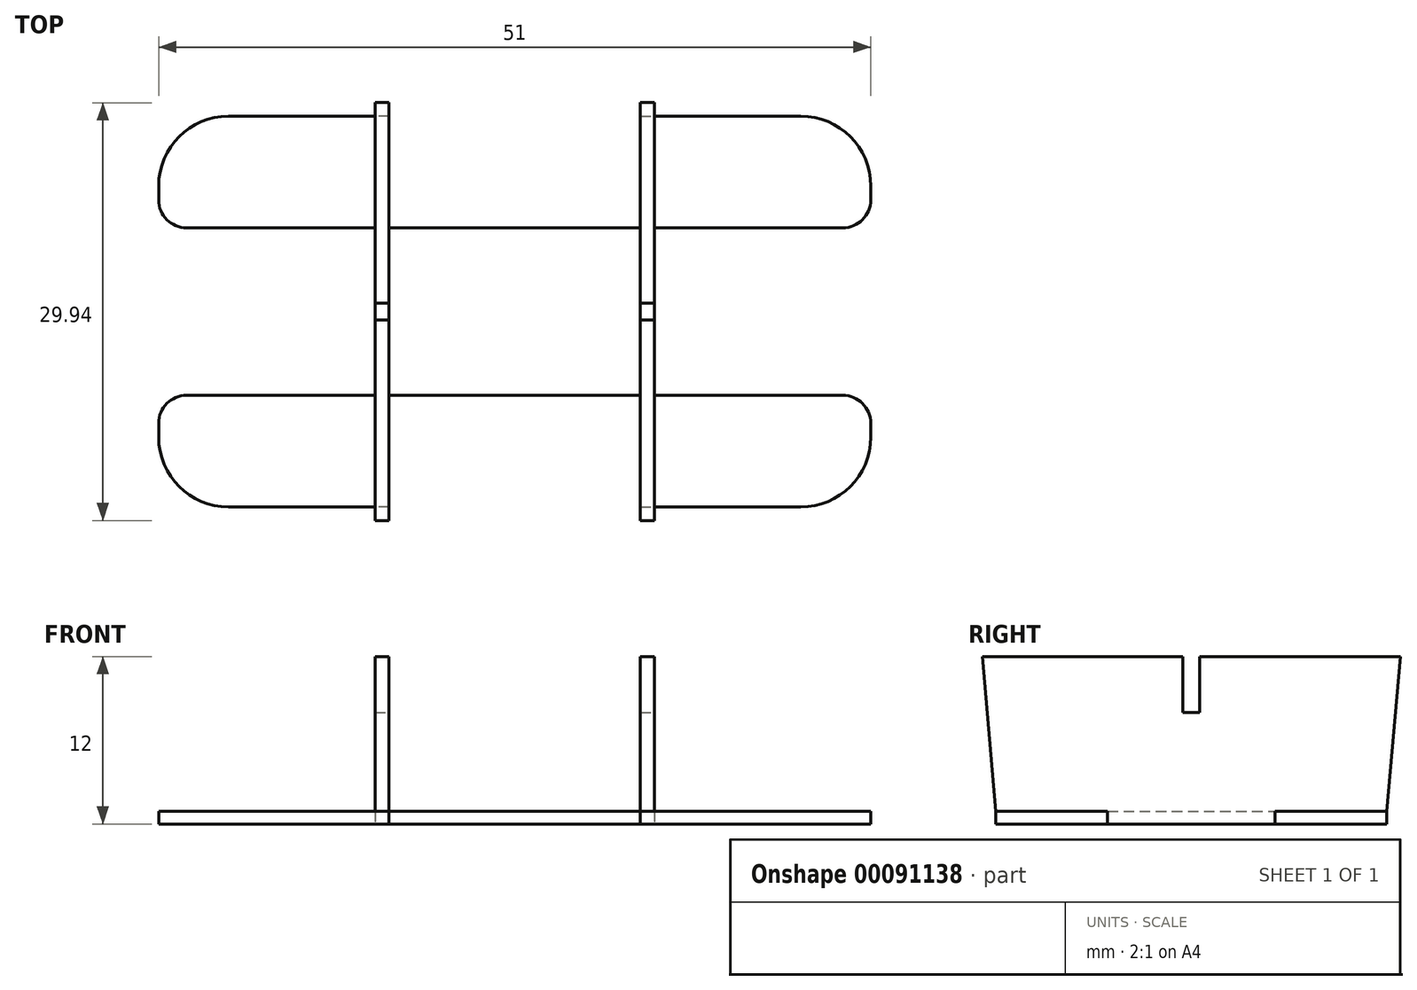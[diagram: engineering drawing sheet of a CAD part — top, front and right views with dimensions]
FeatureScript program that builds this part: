
annotation { "Feature Type Name" : "Feature", "Feature Type Description" : "" }
export const myFeature = defineFeature(function(context is Context, id is Id, definition is map)
    precondition{}
    {
        {
            var Q0;
            Q0=qCreatedBy(makeId("Top.planeOp"),FACE);
            var sketch = newSketch(context, id + "F0", { "sketchPlane" : qUnion([Q0])});
            skLineSegment(sketch, "E0.bottom", {"start": v(-20.5, 14) * mm, "end": v(20.5, 14) * mm});
            skLineSegment(sketch, "E0.top", {"start": v(-20.5, -14) * mm, "end": v(20.5, -14) * mm});
            skLineSegment(sketch, "E0.left", {"start": v(-25.5, 9) * mm, "end": v(-25.5, -9) * mm});
            skLineSegment(sketch, "E0.right", {"start": v(25.5, 9) * mm, "end": v(25.5, -9) * mm});
            skPoint(sketch, "E0.middle", {"position": v(0, 0) * mm});
            skLineSegment(sketch, "E1", {"start": v(-25.5, 6) * mm, "end": v(25.5, 6) * mm});
            skLineSegment(sketch, "E2", {"start": v(25.5, -6) * mm, "end": v(-25.5, -6) * mm});
            skLineSegment(sketch, "E3", {"start": v(-10, 14) * mm, "end": v(-10, -14) * mm});
            skLineSegment(sketch, "E4", {"start": v(10, -14) * mm, "end": v(10, 14) * mm});
            skPoint(sketch, "E5.visualSharp", {"position": v(-25.5, 14) * mm});
            skArc(sketch, "E5.filletArc", {"start": v(-20.5, 14) * mm, "mid": v(-24.04, 12.54) * mm, "end": v(-25.5, 9) * mm});
            skPoint(sketch, "E6.visualSharp", {"position": v(-25.5, -14) * mm});
            skArc(sketch, "E6.filletArc", {"start": v(-25.5, -9) * mm, "mid": v(-24.04, -12.54) * mm, "end": v(-20.5, -14) * mm});
            skPoint(sketch, "E7.visualSharp", {"position": v(25.5, -14) * mm});
            skArc(sketch, "E7.filletArc", {"start": v(20.5, -14) * mm, "mid": v(24.04, -12.54) * mm, "end": v(25.5, -9) * mm});
            skPoint(sketch, "E8.visualSharp", {"position": v(25.5, 14) * mm});
            skArc(sketch, "E8.filletArc", {"start": v(25.5, 9) * mm, "mid": v(24.04, 12.54) * mm, "end": v(20.5, 14) * mm});
            skLineSegment(sketch, "E9", {"start": v(-9, 14) * mm, "end": v(-9, -14) * mm});
            skLineSegment(sketch, "E10", {"start": v(9, -14) * mm, "end": v(9, 14) * mm});
            skSolve(sketch);
        }
        {
            var Q0;
            {var subQ5=sQuery(id+"F0.wireOp",EDGE,"E5.filletArc");Q0=makeQuery(id+"F0.imprint","IMPRINT",FACE,{"disambiguationData":[TD([[makeQuery(id+"F0.imprint","IMPRINT",EDGE,{"derivedFrom":subQ5}),1.0]])]});}
            var Q1;
            {var subQ0=sQuery(id+"F0.wireOp",EDGE,"E3");var subQ1=sQuery(id+"F0.wireOp",EDGE,"E0.bottom");var subQ2=makeQuery(id+"F0.imprint","INTERSECT",VERTEX,{"derivedFrom":[subQ1,subQ0]});Q1=makeQuery(id+"F0.imprint","IMPRINT",FACE,{"disambiguationData":[TD([[makeQuery(id+"F0.imprint","IMPRINT",EDGE,{"disambiguationData":[TD([[subQ2,-1.0]])],"derivedFrom":subQ1}),-1.0]])]});}
            var Q2;
            {var subQ0=sQuery(id+"F0.wireOp",EDGE,"E3");var subQ1=sQuery(id+"F0.wireOp",EDGE,"E1");var subQ2=makeQuery(id+"F0.imprint","INTERSECT",VERTEX,{"derivedFrom":[subQ1,subQ0]});Q2=makeQuery(id+"F0.imprint","IMPRINT",FACE,{"disambiguationData":[TD([[makeQuery(id+"F0.imprint","IMPRINT",EDGE,{"disambiguationData":[TD([[subQ2,-1.0]])],"derivedFrom":subQ1}),-1.0]])]});}
            var Q3;
            {var subQ0=sQuery(id+"F0.wireOp",EDGE,"E3");var subQ1=sQuery(id+"F0.wireOp",EDGE,"E0.top");var subQ2=makeQuery(id+"F0.imprint","INTERSECT",VERTEX,{"derivedFrom":[subQ1,subQ0]});Q3=makeQuery(id+"F0.imprint","IMPRINT",FACE,{"disambiguationData":[TD([[makeQuery(id+"F0.imprint","IMPRINT",EDGE,{"disambiguationData":[TD([[subQ2,-1.0]])],"derivedFrom":subQ1}),1.0]])]});}
            var Q4;
            {var subQ7=sQuery(id+"F0.wireOp",EDGE,"E6.filletArc");Q4=makeQuery(id+"F0.imprint","IMPRINT",FACE,{"disambiguationData":[TD([[makeQuery(id+"F0.imprint","IMPRINT",EDGE,{"derivedFrom":subQ7}),1.0]])]});}
            var Q5;
            {var subQ7=sQuery(id+"F0.wireOp",EDGE,"E7.filletArc");Q5=makeQuery(id+"F0.imprint","IMPRINT",FACE,{"disambiguationData":[TD([[makeQuery(id+"F0.imprint","IMPRINT",EDGE,{"derivedFrom":subQ7}),1.0]])]});}
            var Q6;
            {var subQ5=sQuery(id+"F0.wireOp",EDGE,"E8.filletArc");Q6=makeQuery(id+"F0.imprint","IMPRINT",FACE,{"disambiguationData":[TD([[makeQuery(id+"F0.imprint","IMPRINT",EDGE,{"derivedFrom":subQ5}),1.0]])]});}
            var Q7;
            {var subQ0=sQuery(id+"F0.wireOp",EDGE,"E4");var subQ1=sQuery(id+"F0.wireOp",EDGE,"E0.bottom");var subQ2=makeQuery(id+"F0.imprint","INTERSECT",VERTEX,{"derivedFrom":[subQ1,subQ0]});Q7=makeQuery(id+"F0.imprint","IMPRINT",FACE,{"disambiguationData":[TD([[makeQuery(id+"F0.imprint","IMPRINT",EDGE,{"disambiguationData":[TD([[subQ2,1.0]])],"derivedFrom":subQ1}),-1.0]])]});}
            var Q8;
            {var subQ0=sQuery(id+"F0.wireOp",EDGE,"E10");var subQ1=sQuery(id+"F0.wireOp",EDGE,"E1");var subQ2=makeQuery(id+"F0.imprint","INTERSECT",VERTEX,{"derivedFrom":[subQ1,subQ0]});Q8=makeQuery(id+"F0.imprint","IMPRINT",FACE,{"disambiguationData":[TD([[makeQuery(id+"F0.imprint","IMPRINT",EDGE,{"disambiguationData":[TD([[subQ2,-1.0]])],"derivedFrom":subQ1}),-1.0]])]});}
            var Q9;
            {var subQ0=sQuery(id+"F0.wireOp",EDGE,"E4");var subQ1=sQuery(id+"F0.wireOp",EDGE,"E0.top");var subQ2=makeQuery(id+"F0.imprint","INTERSECT",VERTEX,{"derivedFrom":[subQ1,subQ0]});Q9=makeQuery(id+"F0.imprint","IMPRINT",FACE,{"disambiguationData":[TD([[makeQuery(id+"F0.imprint","IMPRINT",EDGE,{"disambiguationData":[TD([[subQ2,1.0]])],"derivedFrom":subQ1}),1.0]])]});}
            var Q10;
            {var subQ0=sQuery(id+"F0.wireOp",EDGE,"E9");var subQ1=sQuery(id+"F0.wireOp",EDGE,"E1");var subQ2=makeQuery(id+"F0.imprint","INTERSECT",VERTEX,{"derivedFrom":[subQ1,subQ0]});Q10=makeQuery(id+"F0.imprint","IMPRINT",FACE,{"disambiguationData":[TD([[makeQuery(id+"F0.imprint","IMPRINT",EDGE,{"disambiguationData":[TD([[subQ2,-1.0]])],"derivedFrom":subQ1}),-1.0]])]});}
            extrude(context, id + "F1", {"entities" : qUnion([Q0, Q1, Q2, Q3, Q4, Q5, Q6, Q7, Q8, Q9, Q10]), "depth" : .9 * mm});
        }
        {
            var Q0;
            {var subQ0=sQuery(id+"F0.wireOp",EDGE,"E3");var subQ1=sQuery(id+"F0.wireOp",EDGE,"E0.top");var subQ2=makeQuery(id+"F0.imprint","INTERSECT",VERTEX,{"derivedFrom":[subQ1,subQ0]});Q0=makeQuery(id+"F0.imprint","IMPRINT",FACE,{"disambiguationData":[TD([[makeQuery(id+"F0.imprint","IMPRINT",EDGE,{"disambiguationData":[TD([[subQ2,-1.0]])],"derivedFrom":subQ1}),1.0]])]});}
            var Q1;
            {var subQ0=sQuery(id+"F0.wireOp",EDGE,"E3");var subQ1=sQuery(id+"F0.wireOp",EDGE,"E1");var subQ2=makeQuery(id+"F0.imprint","INTERSECT",VERTEX,{"derivedFrom":[subQ1,subQ0]});Q1=makeQuery(id+"F0.imprint","IMPRINT",FACE,{"disambiguationData":[TD([[makeQuery(id+"F0.imprint","IMPRINT",EDGE,{"disambiguationData":[TD([[subQ2,-1.0]])],"derivedFrom":subQ1}),-1.0]])]});}
            var Q2;
            {var subQ0=sQuery(id+"F0.wireOp",EDGE,"E3");var subQ1=sQuery(id+"F0.wireOp",EDGE,"E0.bottom");var subQ2=makeQuery(id+"F0.imprint","INTERSECT",VERTEX,{"derivedFrom":[subQ1,subQ0]});Q2=makeQuery(id+"F0.imprint","IMPRINT",FACE,{"disambiguationData":[TD([[makeQuery(id+"F0.imprint","IMPRINT",EDGE,{"disambiguationData":[TD([[subQ2,-1.0]])],"derivedFrom":subQ1}),-1.0]])]});}
            var Q3;
            {var subQ0=sQuery(id+"F0.wireOp",EDGE,"E4");var subQ1=sQuery(id+"F0.wireOp",EDGE,"E0.bottom");var subQ2=makeQuery(id+"F0.imprint","INTERSECT",VERTEX,{"derivedFrom":[subQ1,subQ0]});Q3=makeQuery(id+"F0.imprint","IMPRINT",FACE,{"disambiguationData":[TD([[makeQuery(id+"F0.imprint","IMPRINT",EDGE,{"disambiguationData":[TD([[subQ2,1.0]])],"derivedFrom":subQ1}),-1.0]])]});}
            var Q4;
            {var subQ0=sQuery(id+"F0.wireOp",EDGE,"E10");var subQ1=sQuery(id+"F0.wireOp",EDGE,"E1");var subQ2=makeQuery(id+"F0.imprint","INTERSECT",VERTEX,{"derivedFrom":[subQ1,subQ0]});Q4=makeQuery(id+"F0.imprint","IMPRINT",FACE,{"disambiguationData":[TD([[makeQuery(id+"F0.imprint","IMPRINT",EDGE,{"disambiguationData":[TD([[subQ2,-1.0]])],"derivedFrom":subQ1}),-1.0]])]});}
            var Q5;
            {var subQ0=sQuery(id+"F0.wireOp",EDGE,"E4");var subQ1=sQuery(id+"F0.wireOp",EDGE,"E0.top");var subQ2=makeQuery(id+"F0.imprint","INTERSECT",VERTEX,{"derivedFrom":[subQ1,subQ0]});Q5=makeQuery(id+"F0.imprint","IMPRINT",FACE,{"disambiguationData":[TD([[makeQuery(id+"F0.imprint","IMPRINT",EDGE,{"disambiguationData":[TD([[subQ2,1.0]])],"derivedFrom":subQ1}),1.0]])]});}
            extrude(context, id + "F2", {"entities" : qUnion([Q0, Q1, Q2, Q3, Q4, Q5]), "operationType" : NewBodyOperationType.ADD, "depth" : 12 * mm});
        }
        {
            var Q0;
            Q0=makeQuery(id+"F1.opExtrude","SWEPT_EDGE",EDGE,{"disambiguationData":[OSD([sQuery(id+"F0.wireOp",EDGE,"E0.left"),sQuery(id+"F0.wireOp",EDGE,"E1")])]});
            var Q1;
            Q1=makeQuery(id+"F1.opExtrude","SWEPT_EDGE",EDGE,{"disambiguationData":[OSD([sQuery(id+"F0.wireOp",EDGE,"E1"),sQuery(id+"F0.wireOp",EDGE,"E3")])]});
            var Q2;
            Q2=makeQuery(id+"F1.opExtrude","SWEPT_EDGE",EDGE,{"disambiguationData":[OSD([sQuery(id+"F0.wireOp",EDGE,"E2"),sQuery(id+"F0.wireOp",EDGE,"E3")])]});
            var Q3;
            Q3=makeQuery(id+"F1.opExtrude","SWEPT_EDGE",EDGE,{"disambiguationData":[OSD([sQuery(id+"F0.wireOp",EDGE,"E0.left"),sQuery(id+"F0.wireOp",EDGE,"E2")])]});
            var Q4;
            Q4=makeQuery(id+"F1.opExtrude","SWEPT_EDGE",EDGE,{"disambiguationData":[OSD([sQuery(id+"F0.wireOp",EDGE,"E1"),sQuery(id+"F0.wireOp",EDGE,"E9")])]});
            var Q5;
            Q5=makeQuery(id+"F1.opExtrude","SWEPT_EDGE",EDGE,{"disambiguationData":[OSD([sQuery(id+"F0.wireOp",EDGE,"E1"),sQuery(id+"F0.wireOp",EDGE,"E10")])]});
            var Q6;
            Q6=makeQuery(id+"F1.opExtrude","SWEPT_EDGE",EDGE,{"disambiguationData":[OSD([sQuery(id+"F0.wireOp",EDGE,"E0.right"),sQuery(id+"F0.wireOp",EDGE,"E1")])]});
            var Q7;
            Q7=makeQuery(id+"F1.opExtrude","SWEPT_EDGE",EDGE,{"disambiguationData":[OSD([sQuery(id+"F0.wireOp",EDGE,"E0.right"),sQuery(id+"F0.wireOp",EDGE,"E2")])]});
            var Q8;
            Q8=makeQuery(id+"F1.opExtrude","SWEPT_EDGE",EDGE,{"disambiguationData":[OSD([sQuery(id+"F0.wireOp",EDGE,"E1"),sQuery(id+"F0.wireOp",EDGE,"E4")])]});
            var Q9;
            Q9=makeQuery(id+"F1.opExtrude","SWEPT_EDGE",EDGE,{"disambiguationData":[OSD([sQuery(id+"F0.wireOp",EDGE,"E2"),sQuery(id+"F0.wireOp",EDGE,"E4")])]});
            var Q10;
            Q10=makeQuery(id+"F1.opExtrude","SWEPT_EDGE",EDGE,{"disambiguationData":[OSD([sQuery(id+"F0.wireOp",EDGE,"E2"),sQuery(id+"F0.wireOp",EDGE,"E10")])]});
            var Q11;
            Q11=makeQuery(id+"F1.opExtrude","SWEPT_EDGE",EDGE,{"disambiguationData":[OSD([sQuery(id+"F0.wireOp",EDGE,"E2"),sQuery(id+"F0.wireOp",EDGE,"E9")])]});
            fillet(context, id + "F3", {"entities" : qUnion([Q0, Q1, Q2, Q3, Q4, Q5, Q6, Q7, Q8, Q9, Q10, Q11]), "radius" : 2 * mm, "tangentPropagation" : true, "allowEdgeOverflow" : false});
        }
        {
            var Q0;
            {var subQ0=sQuery(id+"F0.wireOp",EDGE,"E4");Q0=makeQuery(id+"F2.boolean.opBoolean","MERGE",FACE,{"derivedFrom":[makeQuery(id+"F1.opExtrude","SWEPT_FACE",FACE,{"disambiguationData":[OSD([subQ0])]}),makeQuery(id+"F2.opExtrude","SWEPT_FACE",FACE,{"disambiguationData":[OSD([subQ0])]})]});}
            var sketch = newSketch(context, id + "F4", { "sketchPlane" : qUnion([Q0])});
            skLineSegment(sketch, "E11", {"start": v(-14, 0.9) * mm, "end": v(-14.97, 12) * mm});
            skLineSegment(sketch, "E12", {"start": v(-14.97, 12) * mm, "end": v(-14, 12) * mm});
            skLineSegment(sketch, "E13", {"start": v(-14, 12) * mm, "end": v(-14, 0.9) * mm});
            skLineSegment(sketch, "E14", {"start": v(14, 12) * mm, "end": v(14.97, 12) * mm});
            skLineSegment(sketch, "E15", {"start": v(14.97, 12) * mm, "end": v(14, 0.9) * mm});
            skLineSegment(sketch, "E16", {"start": v(14, 0.9) * mm, "end": v(14, 12) * mm});
            skSolve(sketch);
        }
        {
            var Q0;
            Q0 = qSketchRegion(id + "F4", true);
            extrude(context, id + "F5", {"entities" : qUnion([Q0]), "operationType" : NewBodyOperationType.ADD, "oppositeDirection" : true, "depth" : 1 * mm});
        }
        {
            var Q0;
            {var subQ0=sQuery(id+"F0.wireOp",EDGE,"E3");Q0=makeQuery(id+"F2.boolean.opBoolean","MERGE",FACE,{"derivedFrom":[makeQuery(id+"F1.opExtrude","SWEPT_FACE",FACE,{"disambiguationData":[OSD([subQ0])]}),makeQuery(id+"F2.opExtrude","SWEPT_FACE",FACE,{"disambiguationData":[OSD([subQ0])]})]});}
            var sketch = newSketch(context, id + "F6", { "sketchPlane" : qUnion([Q0])});
            skLineSegment(sketch, "E17", {"start": v(-14, 12) * mm, "end": v(-14.97, 12) * mm});
            skLineSegment(sketch, "E18", {"start": v(-14.97, 12) * mm, "end": v(-14, 0.9) * mm});
            skLineSegment(sketch, "E19", {"start": v(-14, 0.9) * mm, "end": v(-14, 12) * mm});
            skLineSegment(sketch, "E20", {"start": v(14, 12) * mm, "end": v(14.97, 12) * mm});
            skLineSegment(sketch, "E21", {"start": v(14.97, 12) * mm, "end": v(14, 0.9) * mm});
            skLineSegment(sketch, "E22", {"start": v(14, 0.9) * mm, "end": v(14, 12) * mm});
            skSolve(sketch);
        }
        {
            var Q0;
            Q0 = qSketchRegion(id + "F6", true);
            extrude(context, id + "F7", {"entities" : qUnion([Q0]), "operationType" : NewBodyOperationType.ADD, "oppositeDirection" : true, "depth" : 1 * mm});
        }
        {
            var Q0;
            {var subQ0=sQuery(id+"F0.wireOp",EDGE,"E4");Q0=makeQuery(id+"F5.boolean.opBoolean","MERGE",FACE,{"derivedFrom":[makeQuery(id+"F2.boolean.opBoolean","MERGE",FACE,{"derivedFrom":[makeQuery(id+"F1.opExtrude","SWEPT_FACE",FACE,{"disambiguationData":[OSD([subQ0])]}),makeQuery(id+"F2.opExtrude","SWEPT_FACE",FACE,{"disambiguationData":[OSD([subQ0])]})]}),makeQuery(id+"F5.opExtrude","CAP_FACE",FACE,{"disambiguationData":[OSD([sQuery(id+"F4.wireOp",EDGE,"E11"),sQuery(id+"F4.wireOp",EDGE,"E12"),sQuery(id+"F4.wireOp",EDGE,"E13")])],"isStart":true}),makeQuery(id+"F5.opExtrude","CAP_FACE",FACE,{"disambiguationData":[OSD([sQuery(id+"F4.wireOp",EDGE,"E14"),sQuery(id+"F4.wireOp",EDGE,"E15"),sQuery(id+"F4.wireOp",EDGE,"E16")])],"isStart":true})]});}
            var sketch = newSketch(context, id + "F8", { "sketchPlane" : qUnion([Q0])});
            skLineSegment(sketch, "E23.bottom", {"start": v(-0.6, 12) * mm, "end": v(0.6, 12) * mm});
            skLineSegment(sketch, "E23.top", {"start": v(-0.6, 8) * mm, "end": v(0.6, 8) * mm});
            skLineSegment(sketch, "E23.left", {"start": v(-0.6, 12) * mm, "end": v(-0.6, 8) * mm});
            skLineSegment(sketch, "E23.right", {"start": v(0.6, 12) * mm, "end": v(0.6, 8) * mm});
            skSolve(sketch);
        }
        {
            var Q0;
            Q0=makeQuery(id+"F8.imprint","IMPRINT",FACE,{"disambiguationData":[TD([[makeQuery(id+"F8.imprint","IMPRINT",EDGE,{"derivedFrom":sQuery(id+"F8.wireOp",EDGE,"E23.bottom")}),-1.0]])]});
            extrude(context, id + "F9", {"entities" : qUnion([Q0]), "operationType" : NewBodyOperationType.REMOVE, "oppositeDirection" : true, "depth" : 25 * mm});
        }
    });
